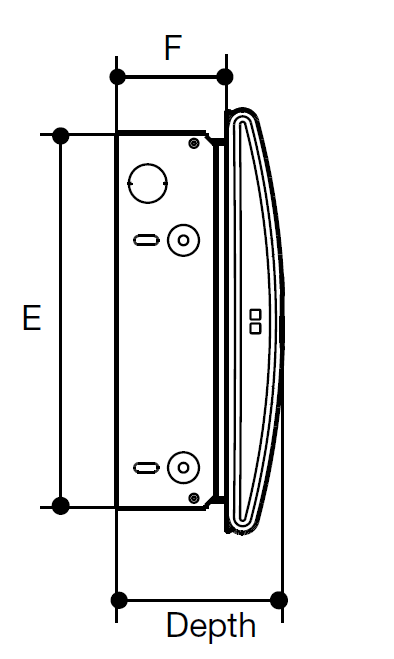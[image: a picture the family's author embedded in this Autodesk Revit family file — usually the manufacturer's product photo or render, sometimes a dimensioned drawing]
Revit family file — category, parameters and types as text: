
# Revit family: Hager-SM_Design_50-Switch_Disc.Incomer-UK-en
name_source: partatom
category: Electrical Equipment
units: mm (PartAtom-declared; Revit-internal decimal feet)

## family parameters
Cut with Voids When Loaded = No
Host = Face
Panel Configuration = Two Columns, Circuits Across
Part Type = Panelboard
Room Calculation Point = No
Round Connector Dimension = Use Diameter
Shared = No

## types (5) — shared parameters
Classification.Uniclass.Pr.Description = Control circuit device enclosures
Classification.Uniclass.Pr.Number = Pr_80_77_28_16
Default Elevation = 11 mm  [stored 0.0360892 ft]
EF000003 - Mounting method = EV000383 - Flush mounted (plaster)
EF000007 - Colour = EV000202 - White
EF000040 - Height = 284 mm  [stored 0.931759 ft]
EF000049 - Depth = 105 mm  [stored 0.344488 ft]
EF000116 - RAL-number = 9010
EF000118 - With mounting plate = No
EF000218 - Built-in depth = 72 mm  [stored 0.23622 ft]
EF000266 - Number of rows = 1
EF000332 - Built-in height = 252 mm  [stored 0.826772 ft]
EF000339 - Type of cover = EV001012 - Cover
EF001062 - EMC-version = No
EF001088 - Extension possible = Yes
EF001134 - DIN-rail = No
EF001596 - Material housing = EV000179 - Steel
EF004462 - Type of closure = EV000154 - Other
EF005474 - Degree of protection (IP) = EV009848 - IP2XC
EF006244 - Transparent cover/door = No
EF006306 - With lock = No
EF009212 - Cover model = EV000116 - Closed
EF015776 - Earthing terminal block = Yes
EF015777 - Neutral terminal block = Yes
EF015941 - Signal passing door = No
Ground Bus = No
HG000002 - With door or cover = Yes
HG000003 - Range = Surface Mounting Consumer Units
HG000005 - Thickness = 3 mm  [stored 0.00984252 ft]
HG000006 - Flush mounted = Yes
HG000017 - Distance between poles = 18 mm  [stored 0.0590551 ft]
Manufacturer = Hager
Neutral Bus = No
Type Comments = Surface Mounting Consumer Units
zero-valued in all types: EF001131 - Internal depth, EF002950 - Width in number of modular spacings

## per-type parameters (varying)
| type | EF000008 - Width | EF000846 - Built-in width | HG000004 - Manufacturer reference | Model |
| Recessed mounted P2XC W359 H284 D105  Modular spacings - VSR110 | 359 mm  [stored 1.17782 ft] | 298 mm  [stored 0.97769 ft] | VSR110 | VSR110 |
| Recessed mounted P2XC W431 H284 D105  Modular spacings - VSR112SPD | 431 mm  [stored 1.41404 ft] | 370 mm  [stored 1.21391 ft] | VSR112SPD | VSR112SPD |
| Recessed mounted P2XC W431 H284 D105  Modular spacings - VSR114 | 431 mm  [stored 1.41404 ft] | 370 mm  [stored 1.21391 ft] | VSR114 | VSR114 |
| Recessed mounted P2XC W539 H284 D105  Modular spacings - VSR118SPD | 539 mm  [stored 1.76837 ft] | 478 mm  [stored 1.56824 ft] | VSR118SPD | VSR118SPD |
| Recessed mounted P2XC W539 H284 D105  Modular spacings - VSR120 | 539 mm  [stored 1.76837 ft] | 478 mm  [stored 1.56824 ft] | VSR120 | VSR120 |

note: [stored X ft] marks values corroborated as IEEE doubles in the binary element streams (Revit-internal decimal feet)

## geometry (parser evidence)
native form markers: Blend x4, Revolve x2, Sweep x13
no freeform markers — native parametric forms only
